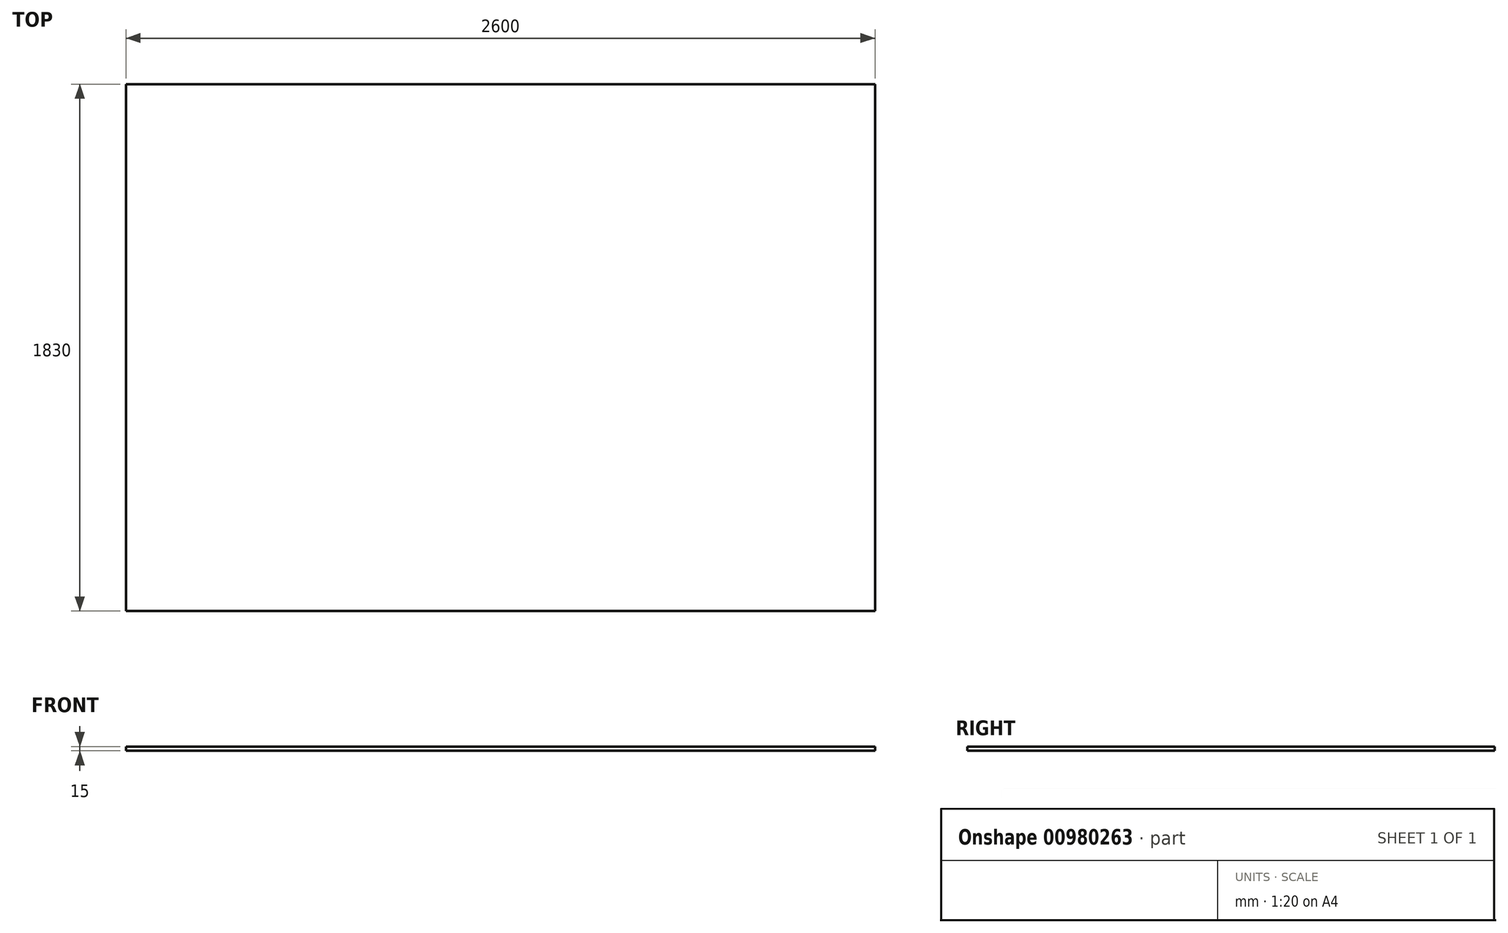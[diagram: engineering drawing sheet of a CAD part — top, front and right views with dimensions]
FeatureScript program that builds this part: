
annotation { "Feature Type Name" : "Feature", "Feature Type Description" : "" }
export const myFeature = defineFeature(function(context is Context, id is Id, definition is map)
    precondition{}
    {
        {
            var Q0;
            Q0=qCreatedBy(makeId("Top.planeOp"),FACE);
            var sketch = newSketch(context, id + "F0", { "sketchPlane" : qUnion([Q0])});
            skLineSegment(sketch, "E0.bottom", {"start": v(-1300, 915) * mm, "end": v(1300, 915) * mm});
            skLineSegment(sketch, "E0.top", {"start": v(-1300, -915) * mm, "end": v(1300, -915) * mm});
            skLineSegment(sketch, "E0.left", {"start": v(-1300, 915) * mm, "end": v(-1300, -915) * mm});
            skLineSegment(sketch, "E0.right", {"start": v(1300, 915) * mm, "end": v(1300, -915) * mm});
            skPoint(sketch, "E0.middle", {"position": v(0, 0) * mm});
            skSolve(sketch);
        }
        {
            var Q0;
            Q0=makeQuery(id+"F0.imprint","IMPRINT",FACE,{"disambiguationData":[TD([[makeQuery(id+"F0.imprint","IMPRINT",EDGE,{"derivedFrom":sQuery(id+"F0.wireOp",EDGE,"E0.bottom")}),-1.0]])]});
            extrude(context, id + "F1", {"entities" : qUnion([Q0]), "depth" : 15 * mm, "offsetDistance" : 25 * mm});
        }
    });
